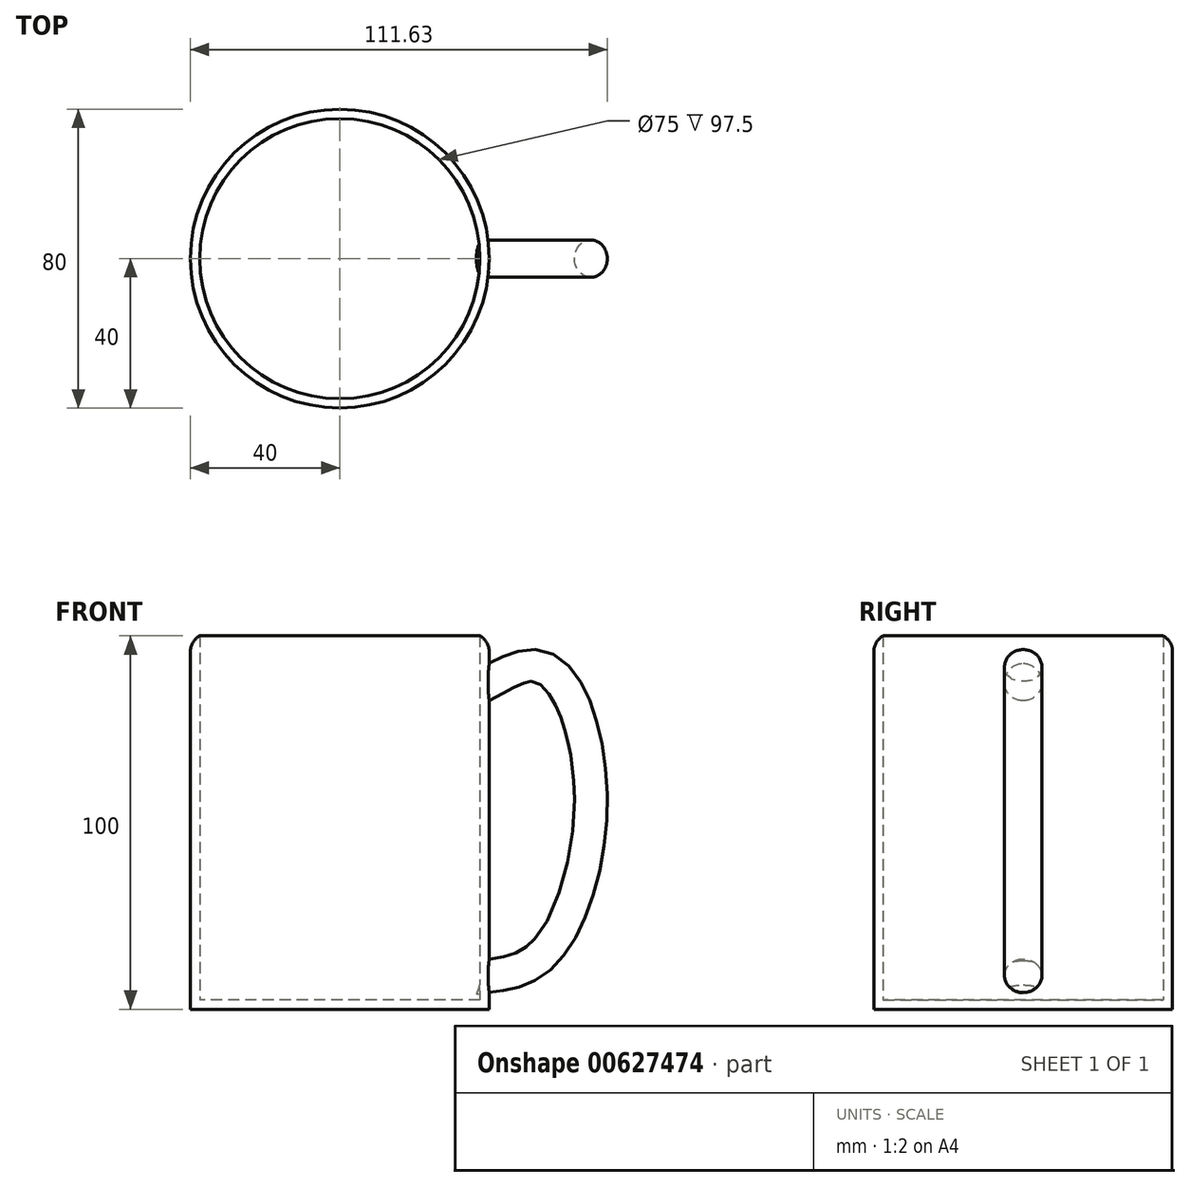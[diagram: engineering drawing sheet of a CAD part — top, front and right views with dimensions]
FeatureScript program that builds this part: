
annotation { "Feature Type Name" : "Feature", "Feature Type Description" : "" }
export const myFeature = defineFeature(function(context is Context, id is Id, definition is map)
    precondition{}
    {
        {
            var Q0;
            Q0=qCreatedBy(makeId("Top.planeOp"),FACE);
            var sketch = newSketch(context, id + "F0", { "sketchPlane" : qUnion([Q0])});
            skCircle(sketch, "E0", {"center": v(0, 0) * mm, "radius": 40 * mm});
            skSolve(sketch);
        }
        {
            var Q0;
            Q0=qCreatedBy(makeId("Front.planeOp"),FACE);
            var sketch = newSketch(context, id + "F1", { "sketchPlane" : qUnion([Q0])});
            skFitSpline(sketch, "E1", {"points": [v(39.5, 86.76) * mm, v(54.89, 90.38) * mm, v(66.66, 56.87) * mm, v(53.98, 15.22) * mm, v(38.58, 9.33) * mm], "startDerivative": vector(84.37, 45.41) * mm, "endDerivative": vector(-82.1, -10.5) * mm});
            skSolve(sketch);
        }
        {
            var Q0;
            Q0=qCreatedBy(makeId("Right.planeOp"),FACE);
            cPlane(context, id + "F2", {"entities" : qUnion([Q0]), "cplaneType" : CPlaneType.OFFSET, "offset" : 40 * mm, "width" : 150 * mm, "height" : 150 * mm});
        }
        {
            var Q0;
            Q0=qCreatedBy(id+"F2.planeOp",FACE);
            var sketch = newSketch(context, id + "F3", { "sketchPlane" : qUnion([Q0])});
            skCircle(sketch, "E2", {"center": v(0, 87.62) * mm, "radius": 5 * mm});
            skCircle(sketch, "E3", {"center": v(0, 9.99) * mm, "radius": 5 * mm});
            skSolve(sketch);
        }
        {
            var Q0;
            Q0 = qSketchRegion(id + "F0", true);
            extrude(context, id + "F4", {"entities" : qUnion([Q0]), "depth" : 100 * mm, "offsetDistance" : 25 * mm});
        }
        {
            var Q0;
            Q0=makeQuery(id+"F4.opExtrude","CAP_FACE",FACE,{"disambiguationData":[OSD([sQuery(id+"F0.wireOp",EDGE,"E0")])],"isStart":false});
            shell(context, id + "F5", {"entities" : qUnion([Q0]), "thickness" : 2.5 * mm});
        }
        {
            var Q0;
            Q0=makeQuery(id+"F3.imprint","IMPRINT",FACE,{"disambiguationData":[TD([[makeQuery(id+"F3.imprint","IMPRINT",EDGE,{"derivedFrom":sQuery(id+"F3.wireOp",EDGE,"E2")}),1.0]])]});
            var Q1;
            Q1=sQuery(id+"F1.wireOp",EDGE,"E1");
            sweep(context, id + "F6", {"operationType" : NewBodyOperationType.ADD, "profiles" : qUnion([Q0]), "path" : qUnion([Q1])});
        }
        {
            var Q0;
            Q0=makeQuery(id+"F4.opExtrude","CAP_EDGE",EDGE,{"disambiguationData":[OSD([sQuery(id+"F0.wireOp",EDGE,"E0")])],"isStart":false});
            fillet(context, id + "F7", {"entities" : qUnion([Q0]), "radius" : 5 * mm, "tangentPropagation" : true, "allowEdgeOverflow" : false});
        }
    });
